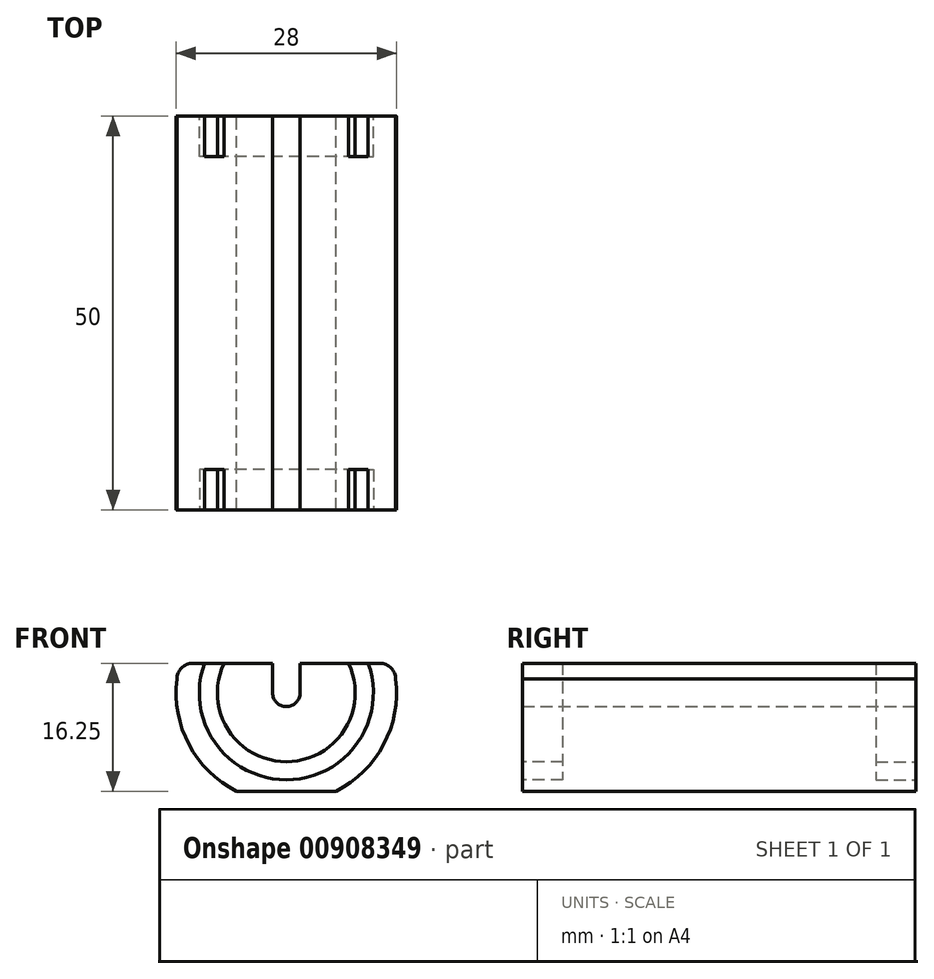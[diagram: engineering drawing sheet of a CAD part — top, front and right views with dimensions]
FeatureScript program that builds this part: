
annotation { "Feature Type Name" : "Feature", "Feature Type Description" : "" }
export const myFeature = defineFeature(function(context is Context, id is Id, definition is map)
    precondition{}
    {
        {
            var Q0;
            Q0=qCreatedBy(makeId("Front.planeOp"),FACE);
            var sketch = newSketch(context, id + "F0", { "sketchPlane" : qUnion([Q0])});
            skArc(sketch, "E0", {"start": v(-13.9, 1.75) * mm, "mid": v(0, -14) * mm, "end": v(13.9, 1.75) * mm});
            skArc(sketch, "E1", {"start": v(-1.75, 0) * mm, "mid": v(0, -1.75) * mm, "end": v(1.75, 0) * mm});
            skLineSegment(sketch, "E2", {"start": v(-13.9, 1.75) * mm, "end": v(-1.75, 1.75) * mm});
            skLineSegment(sketch, "E3", {"start": v(1.75, 0) * mm, "end": v(1.75, 1.75) * mm});
            skLineSegment(sketch, "E4", {"start": v(-1.75, 0) * mm, "end": v(-1.75, 1.75) * mm});
            skLineSegment(sketch, "E5", {"start": v(-6.3, -12.5) * mm, "end": v(6.3, -12.5) * mm});
            skLineSegment(sketch, "E6", {"start": v(13.9, 1.75) * mm, "end": v(13.9, 3.75) * mm});
            skLineSegment(sketch, "E7", {"start": v(1.75, 1.75) * mm, "end": v(1.75, 3.75) * mm});
            skLineSegment(sketch, "E8", {"start": v(-1.75, 1.75) * mm, "end": v(-1.75, 3.75) * mm});
            skLineSegment(sketch, "E9", {"start": v(-13.9, 1.75) * mm, "end": v(-13.9, 3.75) * mm});
            skLineSegment(sketch, "E10", {"start": v(13.9, 3.75) * mm, "end": v(1.75, 3.75) * mm});
            skLineSegment(sketch, "E11.trimOffspring", {"start": v(-1.75, 3.75) * mm, "end": v(-13.9, 3.75) * mm});
            skLineSegment(sketch, "E12.trimOffspring", {"start": v(1.75, 1.75) * mm, "end": v(13.9, 1.75) * mm});
            skSolve(sketch);
        }
        {
            var Q0;
            Q0=makeQuery(id+"F0.imprint","IMPRINT",FACE,{"disambiguationData":[TD([[makeQuery(id+"F0.imprint","IMPRINT",EDGE,{"derivedFrom":sQuery(id+"F0.wireOp",EDGE,"E1")}),-1.0]])]});
            var Q1;
            Q1=makeQuery(id+"F0.imprint","IMPRINT",FACE,{"disambiguationData":[TD([[makeQuery(id+"F0.imprint","IMPRINT",EDGE,{"derivedFrom":sQuery(id+"F0.wireOp",EDGE,"E6")}),1.0]])]});
            var Q2;
            Q2=makeQuery(id+"F0.imprint","IMPRINT",FACE,{"disambiguationData":[TD([[makeQuery(id+"F0.imprint","IMPRINT",EDGE,{"derivedFrom":sQuery(id+"F0.wireOp",EDGE,"E2")}),1.0]])]});
            extrude(context, id + "F1", {"entities" : qUnion([Q0, Q1, Q2]), "depth" : 25 * mm, "offsetDistance" : 25 * mm});
        }
        {
            var Q0;
            Q0=makeQuery(id+"F1.opExtrude","CAP_FACE",FACE,{"disambiguationData":[OSD([sQuery(id+"F0.wireOp",EDGE,"E0"),sQuery(id+"F0.wireOp",EDGE,"E1"),sQuery(id+"F0.wireOp",EDGE,"E2"),sQuery(id+"F0.wireOp",EDGE,"E3"),sQuery(id+"F0.wireOp",EDGE,"E4"),sQuery(id+"F0.wireOp",EDGE,"E5")])],"isStart":true});
            cPlane(context, id + "F2", {"entities" : qUnion([Q0]), "cplaneType" : CPlaneType.OFFSET, "offset" : 3 * mm, "oppositeDirection" : true, "width" : 150 * mm, "height" : 150 * mm});
        }
        {
            var Q0;
            Q0=makeQuery(id+"F1.opExtrude","CAP_FACE",FACE,{"disambiguationData":[OSD([sQuery(id+"F0.wireOp",EDGE,"E0"),sQuery(id+"F0.wireOp",EDGE,"E1"),sQuery(id+"F0.wireOp",EDGE,"E3"),sQuery(id+"F0.wireOp",EDGE,"E4"),sQuery(id+"F0.wireOp",EDGE,"E5"),sQuery(id+"F0.wireOp",EDGE,"E6"),sQuery(id+"F0.wireOp",EDGE,"E7"),sQuery(id+"F0.wireOp",EDGE,"E8"),sQuery(id+"F0.wireOp",EDGE,"E9"),sQuery(id+"F0.wireOp",EDGE,"E10"),sQuery(id+"F0.wireOp",EDGE,"E11.trimOffspring")])],"isStart":true});
            var sketch = newSketch(context, id + "F3", { "sketchPlane" : qUnion([Q0])});
            skCircle(sketch, "E13", {"center": v(0, 0) * mm, "radius": 11.05 * mm});
            skCircle(sketch, "E14", {"center": v(0, 0) * mm, "radius": 8.75 * mm});
            skCircle(sketch, "E15", {"center": v(0, 0) * mm, "radius": 15 * mm});
            skSolve(sketch);
        }
        {
            var Q0;
            {var subQ0=sQuery(id+"F3.wireOp",EDGE,"E13");var subQ1=makeQuery(id+"F1.opExtrude","CAP_EDGE",EDGE,{"disambiguationData":[OSD([sQuery(id+"F0.wireOp",EDGE,"E10")])],"isStart":true});var subQ2=makeQuery(id+"F3.imprint","INTERSECT",VERTEX,{"derivedFrom":[subQ1,subQ0]});Q0=makeQuery(id+"F3.imprint","IMPRINT",FACE,{"disambiguationData":[TD([[makeQuery(id+"F3.imprint","IMPRINT",EDGE,{"disambiguationData":[TD([[subQ2,-1.0]])],"derivedFrom":subQ0}),1.0]])]});}
            extrude(context, id + "F4", {"entities" : qUnion([Q0]), "operationType" : NewBodyOperationType.REMOVE, "oppositeDirection" : true, "depth" : 5.1 * mm, "offsetDistance" : 25 * mm});
        }
        {
            var Q0;
            Q0=qCreatedBy(id+"F2.planeOp",FACE);
            var sketch = newSketch(context, id + "F5", { "sketchPlane" : qUnion([Q0])});
            skCircle(sketch, "E16", {"center": v(0, 0) * mm, "radius": 6.5 * mm});
            skLineSegment(sketch, "E17", {"start": v(6.5, 0) * mm, "end": v(6.5, 8.9) * mm});
            skLineSegment(sketch, "E18", {"start": v(6.5, 8.9) * mm, "end": v(-6.5, 0) * mm});
            skLineSegment(sketch, "E19", {"start": v(-6.5, 0) * mm, "end": v(-6.5, 9.43) * mm});
            skLineSegment(sketch, "E20", {"start": v(-6.5, 9.43) * mm, "end": v(6.5, 8.9) * mm});
            skSolve(sketch);
        }
        {
            var Q0;
            Q0=makeQuery(id+"F1.opExtrude","CAP_FACE",FACE,{"disambiguationData":[OSD([sQuery(id+"F0.wireOp",EDGE,"E0"),sQuery(id+"F0.wireOp",EDGE,"E1"),sQuery(id+"F0.wireOp",EDGE,"E3"),sQuery(id+"F0.wireOp",EDGE,"E4"),sQuery(id+"F0.wireOp",EDGE,"E5"),sQuery(id+"F0.wireOp",EDGE,"E6"),sQuery(id+"F0.wireOp",EDGE,"E7"),sQuery(id+"F0.wireOp",EDGE,"E8"),sQuery(id+"F0.wireOp",EDGE,"E9"),sQuery(id+"F0.wireOp",EDGE,"E10"),sQuery(id+"F0.wireOp",EDGE,"E11.trimOffspring")])],"isStart":true});
            var sketch = newSketch(context, id + "F6", { "sketchPlane" : qUnion([Q0])});
            skCircle(sketch, "E21", {"center": v(0, 0) * mm, "radius": 5.36 * mm});
            skSolve(sketch);
        }
        {
            var Q0;
            Q0=makeQuery(id+"F1.opExtrude","SWEPT_BODY",BODY,{"disambiguationData":[OSD([sQuery(id+"F0.wireOp",EDGE,"E0"),sQuery(id+"F0.wireOp",EDGE,"E1"),sQuery(id+"F0.wireOp",EDGE,"E3"),sQuery(id+"F0.wireOp",EDGE,"E4"),sQuery(id+"F0.wireOp",EDGE,"E5"),sQuery(id+"F0.wireOp",EDGE,"E6"),sQuery(id+"F0.wireOp",EDGE,"E7"),sQuery(id+"F0.wireOp",EDGE,"E8"),sQuery(id+"F0.wireOp",EDGE,"E9"),sQuery(id+"F0.wireOp",EDGE,"E10"),sQuery(id+"F0.wireOp",EDGE,"E11.trimOffspring")])]});
            var Q1;
            Q1=makeQuery(id+"F1.opExtrude","CAP_FACE",FACE,{"disambiguationData":[OSD([sQuery(id+"F0.wireOp",EDGE,"E0"),sQuery(id+"F0.wireOp",EDGE,"E1"),sQuery(id+"F0.wireOp",EDGE,"E3"),sQuery(id+"F0.wireOp",EDGE,"E4"),sQuery(id+"F0.wireOp",EDGE,"E5"),sQuery(id+"F0.wireOp",EDGE,"E6"),sQuery(id+"F0.wireOp",EDGE,"E7"),sQuery(id+"F0.wireOp",EDGE,"E8"),sQuery(id+"F0.wireOp",EDGE,"E9"),sQuery(id+"F0.wireOp",EDGE,"E10"),sQuery(id+"F0.wireOp",EDGE,"E11.trimOffspring")])],"isStart":false});
            mirror(context, id + "F7", {"operationType" : NewBodyOperationType.ADD, "entities" : qUnion([Q0]), "mirrorPlane" : qUnion([Q1])});
        }
        {
            var Q0;
            {var subQ0=makeQuery(id+"F1.opExtrude","SWEPT_EDGE",EDGE,{"disambiguationData":[OSD([sQuery(id+"F0.wireOp",EDGE,"E6"),sQuery(id+"F0.wireOp",EDGE,"E10")])]});Q0=makeQuery(id+"F7.boolean.opBoolean","MERGE",EDGE,{"derivedFrom":[subQ0,makeQuery(id+"F7.opPattern","COPY",EDGE,{"derivedFrom":subQ0,"instanceName":"1"})]});}
            var Q1;
            {var subQ0=makeQuery(id+"F1.opExtrude","SWEPT_EDGE",EDGE,{"disambiguationData":[OSD([sQuery(id+"F0.wireOp",EDGE,"E9"),sQuery(id+"F0.wireOp",EDGE,"E11.trimOffspring")])]});Q1=makeQuery(id+"F7.boolean.opBoolean","MERGE",EDGE,{"derivedFrom":[subQ0,makeQuery(id+"F7.opPattern","COPY",EDGE,{"derivedFrom":subQ0,"instanceName":"1"})]});}
            fillet(context, id + "F8", {"entities" : qUnion([Q0, Q1]), "radius" : 2 * mm, "tangentPropagation" : true, "allowEdgeOverflow" : false});
        }
    });
